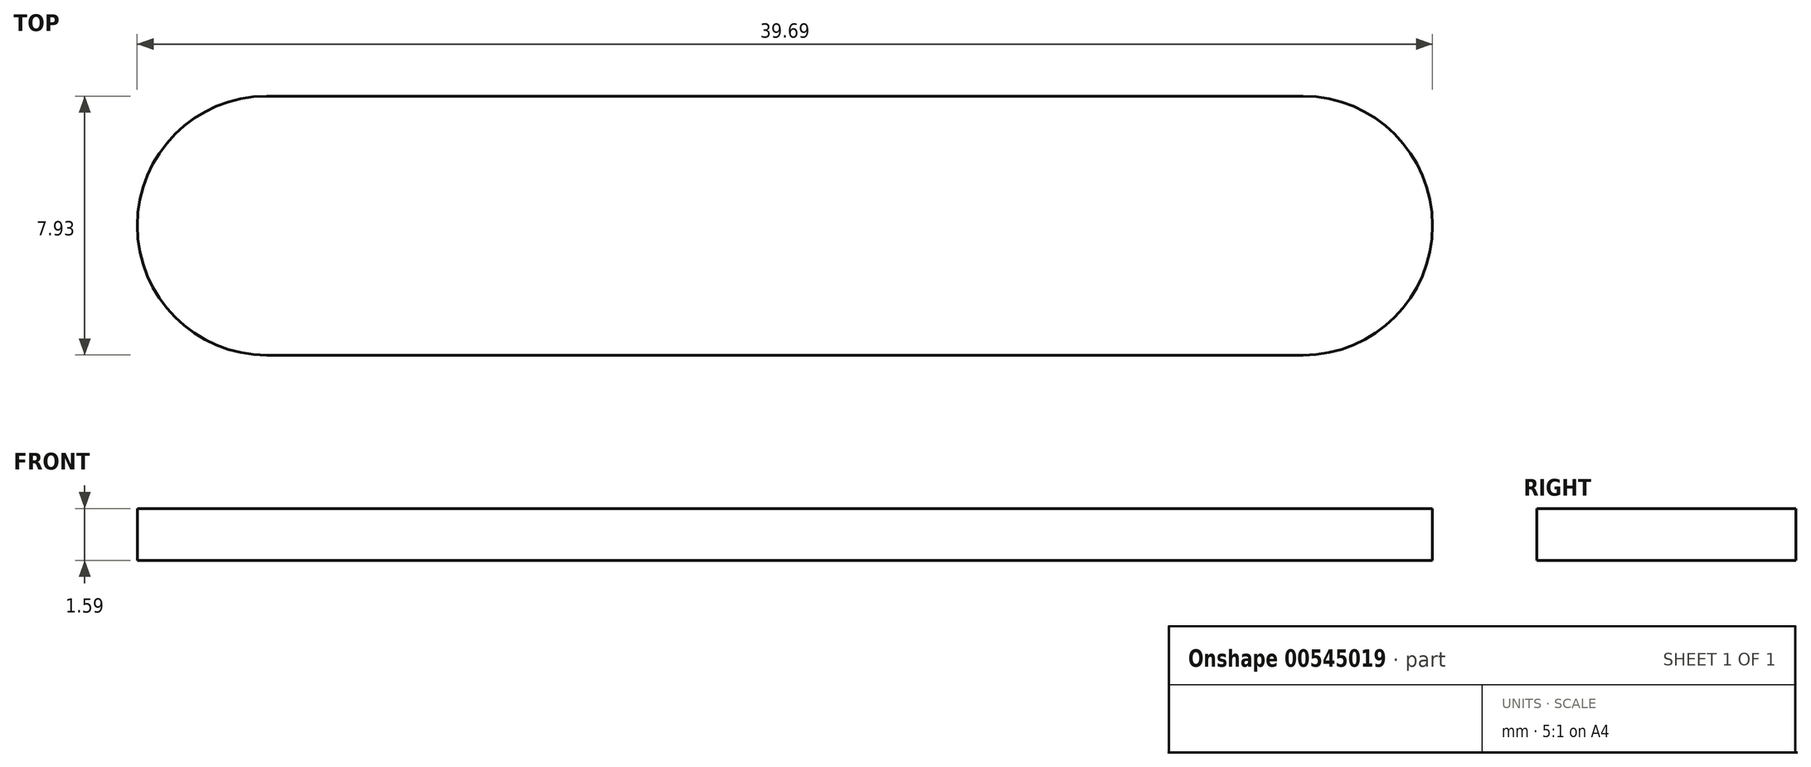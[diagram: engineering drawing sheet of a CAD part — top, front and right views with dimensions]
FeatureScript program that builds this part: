
annotation { "Feature Type Name" : "Feature", "Feature Type Description" : "" }
export const myFeature = defineFeature(function(context is Context, id is Id, definition is map)
    precondition{}
    {
        {
            var Q0;
            Q0=qCreatedBy(makeId("Top.planeOp"),FACE);
            var sketch = newSketch(context, id + "F0", { "sketchPlane" : qUnion([Q0])});
            skLineSegment(sketch, "E0", {"start": v(0, 0) * mm, "end": v(98.43, 0) * mm});
            skLineSegment(sketch, "E1", {"start": v(98.43, 0) * mm, "end": v(98.43, 46.39) * mm});
            skLineSegment(sketch, "E2", {"start": v(98.43, 46.39) * mm, "end": v(14.29, 46.39) * mm});
            skLineSegment(sketch, "E3", {"start": v(14.29, 46.39) * mm, "end": v(14.29, 98.43) * mm});
            skLineSegment(sketch, "E4", {"start": v(14.29, 98.43) * mm, "end": v(31.75, 98.43) * mm});
            skLineSegment(sketch, "E5", {"start": v(31.75, 98.43) * mm, "end": v(31.75, 123.83) * mm, "construction": true});
            skLineSegment(sketch, "E6", {"start": v(31.75, 123.83) * mm, "end": v(0, 123.83) * mm});
            skLineSegment(sketch, "E7", {"start": v(0, 123.83) * mm, "end": v(0, 0) * mm});
            skArc(sketch, "E8", {"start": v(31.75, 123.83) * mm, "mid": v(44.45, 111.13) * mm, "end": v(31.75, 98.43) * mm});
            skCircle(sketch, "E9", {"center": v(31.75, 111.13) * mm, "radius": 1.59 * mm});
            skLineSegment(sketch, "E10", {"start": v(39.69, 35.28) * mm, "end": v(71.44, 35.28) * mm, "construction": true});
            skArc(sketch, "E11.0.startCap", {"start": v(39.69, 31.3) * mm, "mid": v(35.72, 35.28) * mm, "end": v(39.69, 39.25) * mm});
            skArc(sketch, "E11.0.endCap", {"start": v(71.44, 39.25) * mm, "mid": v(75.4, 35.28) * mm, "end": v(71.44, 31.3) * mm});
            skLineSegment(sketch, "E11.0.left", {"start": v(39.69, 39.25) * mm, "end": v(71.44, 39.25) * mm});
            skLineSegment(sketch, "E11.0.right", {"start": v(39.69, 31.3) * mm, "end": v(71.44, 31.3) * mm});
            skLineSegment(sketch, "E12", {"start": v(39.69, 10.32) * mm, "end": v(71.44, 10.32) * mm, "construction": true});
            skArc(sketch, "E13.0.startCap", {"start": v(39.69, 6.35) * mm, "mid": v(35.72, 10.32) * mm, "end": v(39.69, 14.29) * mm});
            skArc(sketch, "E13.0.endCap", {"start": v(71.44, 14.29) * mm, "mid": v(75.4, 10.32) * mm, "end": v(71.44, 6.35) * mm});
            skLineSegment(sketch, "E13.0.left", {"start": v(39.69, 14.29) * mm, "end": v(71.44, 14.29) * mm});
            skLineSegment(sketch, "E13.0.right", {"start": v(39.69, 6.35) * mm, "end": v(71.44, 6.35) * mm});
            skLineSegment(sketch, "E14", {"start": v(0, 88.28) * mm, "end": v(0, 56.53) * mm, "construction": true});
            skArc(sketch, "E15.0.startCap", {"start": v(-3.97, 88.28) * mm, "mid": v(0, 92.25) * mm, "end": v(3.97, 88.28) * mm});
            skArc(sketch, "E15.0.endCap", {"start": v(3.97, 56.53) * mm, "mid": v(0, 52.56) * mm, "end": v(-3.97, 56.53) * mm});
            skLineSegment(sketch, "E15.0.left", {"start": v(3.97, 88.28) * mm, "end": v(3.97, 56.53) * mm});
            skLineSegment(sketch, "E15.0.right", {"start": v(-3.97, 88.28) * mm, "end": v(-3.97, 56.53) * mm});
            skLineSegment(sketch, "E16", {"start": v(14.29, 72.4) * mm, "end": v(0, 72.4) * mm, "construction": true});
            skSolve(sketch);
        }
        {
            var Q0;
            {var subQ1=sQuery(id+"F0.wireOp",EDGE,"E0");Q0=makeQuery(id+"F0.imprint","IMPRINT",FACE,{"disambiguationData":[TD([[makeQuery(id+"F0.imprint","IMPRINT",EDGE,{"derivedFrom":subQ1}),1.0]])]});}
            var Q1;
            Q1=makeQuery(id+"F0.imprint","IMPRINT",FACE,{"disambiguationData":[TD([[makeQuery(id+"F0.imprint","IMPRINT",EDGE,{"derivedFrom":sQuery(id+"F0.wireOp",EDGE,"E11.0.startCap")}),-1.0]])]});
            var Q2;
            Q2=makeQuery(id+"F0.imprint","IMPRINT",FACE,{"disambiguationData":[TD([[makeQuery(id+"F0.imprint","IMPRINT",EDGE,{"derivedFrom":sQuery(id+"F0.wireOp",EDGE,"E13.0.startCap")}),-1.0]])]});
            extrude(context, id + "F1", {"entities" : qUnion([Q0, Q1, Q2]), "depth" : 1.59 * mm, "offsetDistance" : 25.4 * mm});
        }
        {
            var Q0;
            Q0=makeQuery(id+"F1.opExtrude","SWEPT_EDGE",EDGE,{"disambiguationData":[OSD([sQuery(id+"F0.wireOp",EDGE,"E3"),sQuery(id+"F0.wireOp",EDGE,"E4")])]});
            var Q1;
            Q1=makeQuery(id+"F1.opExtrude","SWEPT_EDGE",EDGE,{"disambiguationData":[OSD([sQuery(id+"F0.wireOp",EDGE,"E2"),sQuery(id+"F0.wireOp",EDGE,"E3")])]});
            var Q2;
            Q2=makeQuery(id+"F1.opExtrude","SWEPT_EDGE",EDGE,{"disambiguationData":[OSD([sQuery(id+"F0.wireOp",EDGE,"E1"),sQuery(id+"F0.wireOp",EDGE,"E2")])]});
            var Q3;
            Q3=makeQuery(id+"F1.opExtrude","SWEPT_EDGE",EDGE,{"disambiguationData":[OSD([sQuery(id+"F0.wireOp",EDGE,"E0"),sQuery(id+"F0.wireOp",EDGE,"E1")])]});
            fillet(context, id + "F2", {"entities" : qUnion([Q0, Q1, Q2, Q3]), "radius" : 0.8 * mm, "tangentPropagation" : true, "allowEdgeOverflow" : false});
        }
        {
            var Q0;
            Q0=makeQuery(id+"F1.opExtrude","SWEPT_BODY",BODY,{"disambiguationData":[OSD([sQuery(id+"F0.wireOp",EDGE,"E0"),sQuery(id+"F0.wireOp",EDGE,"E1"),sQuery(id+"F0.wireOp",EDGE,"E2"),sQuery(id+"F0.wireOp",EDGE,"E3"),sQuery(id+"F0.wireOp",EDGE,"E4"),sQuery(id+"F0.wireOp",EDGE,"E6"),sQuery(id+"F0.wireOp",EDGE,"E7"),sQuery(id+"F0.wireOp",EDGE,"E8"),sQuery(id+"F0.wireOp",EDGE,"E9"),sQuery(id+"F0.wireOp",EDGE,"E11.0.startCap"),sQuery(id+"F0.wireOp",EDGE,"E11.0.endCap"),sQuery(id+"F0.wireOp",EDGE,"E11.0.left"),sQuery(id+"F0.wireOp",EDGE,"E11.0.right"),sQuery(id+"F0.wireOp",EDGE,"E13.0.startCap"),sQuery(id+"F0.wireOp",EDGE,"E13.0.endCap"),sQuery(id+"F0.wireOp",EDGE,"E13.0.left"),sQuery(id+"F0.wireOp",EDGE,"E13.0.right")])]});
            var Q1;
            Q1=qCreatedBy(makeId("Right.planeOp"),FACE);
            mirror(context, id + "F3", {"operationType" : NewBodyOperationType.ADD, "entities" : qUnion([Q0]), "mirrorPlane" : qUnion([Q1])});
        }
        {
            var Q0;
            {var subQ0=makeQuery(id+"F1.opExtrude","CAP_FACE",FACE,{"disambiguationData":[OSD([sQuery(id+"F0.wireOp",EDGE,"E0"),sQuery(id+"F0.wireOp",EDGE,"E1"),sQuery(id+"F0.wireOp",EDGE,"E2"),sQuery(id+"F0.wireOp",EDGE,"E3"),sQuery(id+"F0.wireOp",EDGE,"E4"),sQuery(id+"F0.wireOp",EDGE,"E6"),sQuery(id+"F0.wireOp",EDGE,"E7"),sQuery(id+"F0.wireOp",EDGE,"E8"),sQuery(id+"F0.wireOp",EDGE,"E9"),sQuery(id+"F0.wireOp",EDGE,"E15.0.startCap"),sQuery(id+"F0.wireOp",EDGE,"E15.0.endCap"),sQuery(id+"F0.wireOp",EDGE,"E15.0.left")])],"isStart":false});Q0=makeQuery(id+"F3.boolean.opBoolean","MERGE",FACE,{"derivedFrom":[subQ0,makeQuery(id+"F3.opPattern","COPY",FACE,{"derivedFrom":subQ0,"instanceName":"1"})]});}
            var sketch = newSketch(context, id + "F4", { "sketchPlane" : qUnion([Q0])});
            skLineSegment(sketch, "E17.0", {"start": v(39.69, 39.25) * mm, "end": v(71.44, 39.25) * mm});
            skArc(sketch, "E18.0", {"start": v(39.69, 31.3) * mm, "mid": v(35.72, 35.28) * mm, "end": v(39.69, 39.25) * mm});
            skLineSegment(sketch, "E19.0", {"start": v(39.69, 31.3) * mm, "end": v(71.44, 31.3) * mm});
            skArc(sketch, "E20.0", {"start": v(71.44, 39.25) * mm, "mid": v(75.4, 35.28) * mm, "end": v(71.44, 31.3) * mm});
            skArc(sketch, "E21.0", {"start": v(39.69, 6.35) * mm, "mid": v(35.72, 10.32) * mm, "end": v(39.69, 14.29) * mm});
            skLineSegment(sketch, "E22.0", {"start": v(39.69, 14.29) * mm, "end": v(71.44, 14.29) * mm});
            skArc(sketch, "E23.0", {"start": v(71.44, 14.29) * mm, "mid": v(75.4, 10.32) * mm, "end": v(71.44, 6.35) * mm});
            skLineSegment(sketch, "E24.0", {"start": v(39.69, 6.35) * mm, "end": v(71.44, 6.35) * mm});
            skLineSegment(sketch, "E25", {"start": v(-71.44, 23.2) * mm, "end": v(-39.69, 23.2) * mm, "construction": true});
            skPoint(sketch, "E25.startSnap0", {"position": v(-98.43, 23.2) * mm});
            skArc(sketch, "E26.0.startCap", {"start": v(-71.44, 19.23) * mm, "mid": v(-75.4, 23.2) * mm, "end": v(-71.44, 27.16) * mm});
            skArc(sketch, "E26.0.endCap", {"start": v(-39.69, 27.16) * mm, "mid": v(-35.72, 23.2) * mm, "end": v(-39.69, 19.23) * mm});
            skLineSegment(sketch, "E26.0.left", {"start": v(-71.44, 27.16) * mm, "end": v(-39.69, 27.16) * mm});
            skLineSegment(sketch, "E26.0.right", {"start": v(-71.44, 19.23) * mm, "end": v(-39.69, 19.23) * mm});
            skLineSegment(sketch, "E27", {"start": v(-98.43, 23.2) * mm, "end": v(-71.44, 23.2) * mm, "construction": true});
            skLineSegment(sketch, "E28", {"start": v(71.44, 35.28) * mm, "end": v(98.43, 35.28) * mm, "construction": true});
            skSolve(sketch);
        }
        {
            var Q0;
            Q0=makeQuery(id+"F4.imprint","IMPRINT",FACE,{"disambiguationData":[TD([[makeQuery(id+"F4.imprint","IMPRINT",EDGE,{"derivedFrom":sQuery(id+"F4.wireOp",EDGE,"E26.0.startCap")}),-1.0]])]});
            var Q1;
            Q1=makeQuery(id+"F4.imprint","IMPRINT",FACE,{"disambiguationData":[TD([[makeQuery(id+"F4.imprint","IMPRINT",EDGE,{"derivedFrom":sQuery(id+"F4.wireOp",EDGE,"E17.0")}),-1.0]])]});
            var Q2;
            Q2=makeQuery(id+"F4.imprint","IMPRINT",FACE,{"disambiguationData":[TD([[makeQuery(id+"F4.imprint","IMPRINT",EDGE,{"derivedFrom":sQuery(id+"F4.wireOp",EDGE,"E21.0")}),-1.0]])]});
            extrude(context, id + "F5", {"entities" : qUnion([Q0, Q1, Q2]), "operationType" : NewBodyOperationType.REMOVE, "endBound" : BoundingType.THROUGH_ALL, "oppositeDirection" : true, "depth" : 25.4 * mm, "offsetDistance" : 25.4 * mm});
        }
    });
